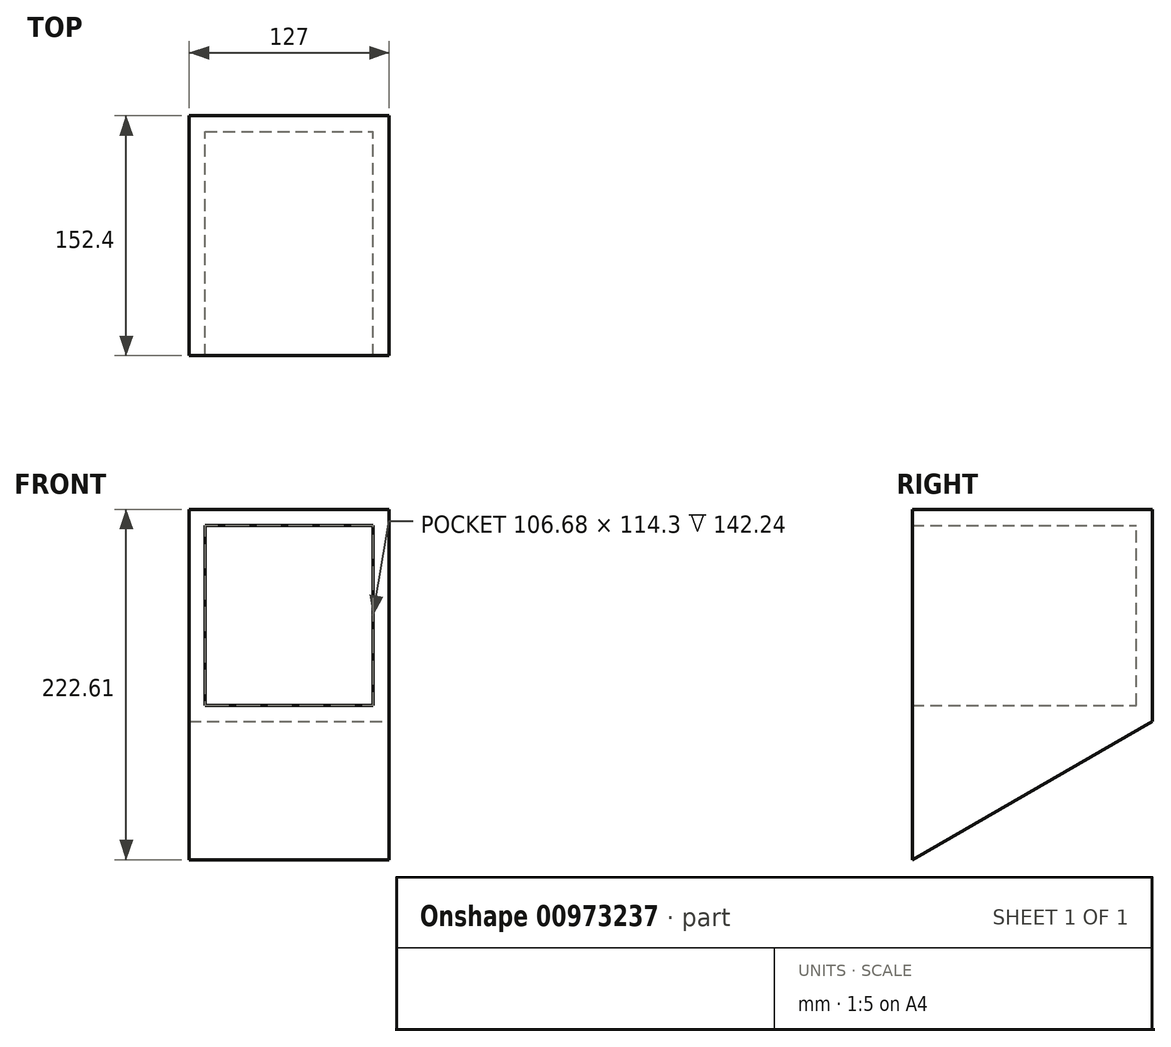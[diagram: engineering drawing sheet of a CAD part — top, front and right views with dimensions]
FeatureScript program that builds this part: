
annotation { "Feature Type Name" : "Feature", "Feature Type Description" : "" }
export const myFeature = defineFeature(function(context is Context, id is Id, definition is map)
    precondition{}
    {
        {
            var Q0;
            Q0=qCreatedBy(makeId("Front.planeOp"),FACE);
            var sketch = newSketch(context, id + "F0", { "sketchPlane" : qUnion([Q0])});
            skLineSegment(sketch, "E0.bottom", {"start": v(0, 0) * mm, "end": v(127, 0) * mm});
            skLineSegment(sketch, "E0.top", {"start": v(0, 134.62) * mm, "end": v(127, 134.62) * mm});
            skLineSegment(sketch, "E0.left", {"start": v(0, 0) * mm, "end": v(0, 134.62) * mm});
            skLineSegment(sketch, "E0.right", {"start": v(127, 0) * mm, "end": v(127, 134.62) * mm});
            skSolve(sketch);
        }
        {
            var Q0;
            Q0=makeQuery(id+"F0.imprint","IMPRINT",FACE,{"disambiguationData":[TD([[makeQuery(id+"F0.imprint","IMPRINT",EDGE,{"derivedFrom":sQuery(id+"F0.wireOp",EDGE,"E0.bottom")}),1.0]])]});
            extrude(context, id + "F1", {"entities" : qUnion([Q0]), "depth" : 152.4 * mm, "offsetDistance" : 25.4 * mm});
        }
        {
            var Q0;
            Q0=makeQuery(id+"F1.opExtrude","CAP_FACE",FACE,{"disambiguationData":[OSD([sQuery(id+"F0.wireOp",EDGE,"E0.bottom"),sQuery(id+"F0.wireOp",EDGE,"E0.top"),sQuery(id+"F0.wireOp",EDGE,"E0.left"),sQuery(id+"F0.wireOp",EDGE,"E0.right")])],"isStart":false});
            shell(context, id + "F2", {"entities" : qUnion([Q0]), "thickness" : 10.16 * mm});
        }
        {
            var Q0;
            Q0=qCreatedBy(makeId("Right.planeOp"),FACE);
            var sketch = newSketch(context, id + "F3", { "sketchPlane" : qUnion([Q0])});
            skLineSegment(sketch, "E1", {"start": v(0, 0) * mm, "end": v(-152.4, -87.99) * mm});
            skLineSegment(sketch, "E2", {"start": v(-152.4, -87.99) * mm, "end": v(-152.4, 0) * mm});
            skLineSegment(sketch, "E3", {"start": v(0, 0) * mm, "end": v(-152.4, 0) * mm});
            skSolve(sketch);
        }
        {
            var Q0;
            Q0 = qSketchRegion(id + "F3", true);
            var Q1;
            Q1=makeQuery(id+"F1.opExtrude","SWEPT_FACE",FACE,{"disambiguationData":[OSD([sQuery(id+"F0.wireOp",EDGE,"E0.right")])]});
            extrude(context, id + "F4", {"entities" : qUnion([Q0]), "operationType" : NewBodyOperationType.ADD, "endBound" : BoundingType.UP_TO_SURFACE, "depth" : 25.4 * mm, "endBoundEntityFace" : qUnion([Q1]), "offsetDistance" : 25.4 * mm});
        }
    });
